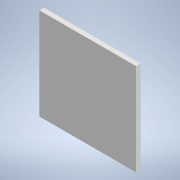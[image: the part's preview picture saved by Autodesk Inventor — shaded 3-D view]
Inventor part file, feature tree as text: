
AUTODESK INVENTOR PART (.ipt)
format: ipt  version: 2022 (Build 260153000, 153)  size: 88,576 bytes
history: native  units: mm
features: extrude x1, sketch x1
ambient origin geometry x8: Origin, YZ Plane, XZ Plane, XY Plane, X Axis, Y Axis, Z Axis, Center Point
bodies: Solid1 (feature_tree)
feature tree (2):
  extrude  "Extrusion1"  Depth=100.0mm
  sketch  "Sketch1"  dims[d0=105.0mm d1=100.0mm d2=5.0mm d3=0.0mm]
